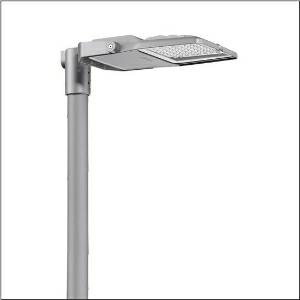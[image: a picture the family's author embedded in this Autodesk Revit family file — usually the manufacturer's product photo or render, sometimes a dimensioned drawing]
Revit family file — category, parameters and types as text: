
# Revit family: floodlight_fl_21_mini___pl43_5xa7772b4a3a_ae29
name_source: partatom
category: Lighting Fixtures
units: mm (PartAtom-declared; Revit-internal decimal feet)

## family parameters
Cut with Voids When Loaded = No
Host = Face
Light Source = No
Part Type = Normal
Room Calculation Point = No
Round Connector Dimension = Use Diameter
Shared = No

## types (1)
- --- (1 x LED, 6660 lm, 45.5 W, 4000K)
    Apparent Load = 46 VA
    CIE Flux Codes = 27 78 99 100 100
    Color Rendering = 70
    Color Temperature = 4000K
    Default Elevation = 1800 mm
    Description = Floodlight FL 21 mini, floodlight, primary light control with lens, of PMMA, primary optical cover: protective disc, of toughened safety glass, transparent, light distribution: PL43, light emission: direct distribution, installation type: surface-mounted, LED, High Power LED, rated luminous flux: 6.660lm, luminous efficacy: 146lm/W, light colour: 740, colour temperature: 4000K, control gear: ECG iQ, control: Auto-Match, Temp-Guard, Night-Set, Smart-Wire, Desk-Remote (wireless, voltage-free reading and setting of iQ features in the workshop via application-optimized NFC function/RFID function), optimised constant luminous flux control (CLO 2.0), Light-Fading, Lumen-Switch, with terminal, 6-pole, mains connection: 220..240V, AC, 50/60Hz, start of lifetime: 46W, end of lifetime: 48W, reduction: 22W, luminaire housing, of diecast aluminium, powder-coated, Siteco® metallic grey (DB 702S), corrosivity category C5 according to DIN EN ISO 12944, mast bracket, of steel, galvanised, powder-coated, protection rating (complete): IP66, insulation class (complete): insulation class II (safety insulation), certification: CE, ENEC, VDE, protection symbol: D, impact resistance: IK08, permissible operating ambient temperature: -40..+40°C, permissible operating ambient temperature for outdoor applications: -40..+50°C, standard: DIN EN 12944, packaging unit: 1 piece

Light Distribution: PL43
    Height = 70 mm
    Lamp = 1 x LED
    Lamp Light Flux = 6660 lm
    Lamp Power = 45.5 W
    Lamp count = 1
    Length = 485 mm
    Luminous efficacy = 146 lm/W
    Manufacturer = Siteco
    ModVariant = No
    Model = 5XA7772B4A3A
    Number of Poles = 1
    OnlyDefault = Yes
    Power Factor = 1
    Product Name = Floodlight FL 21 mini | PL43
    Product group = floodlight | pylon top
    ProductGroupID = 6101
    Protection Class = Protection class II
    Protection Degree = IP 66
    RLX_Detail_Level = 1
    RlxData = <blob elided: 100881 chars, md5=e329fee6>
    Socket = socket
    Standby Power = 0 W
    System Light Flux = 6660 lm
    System Power = 46 W
    Type Comments = factory setting: luminous flux: 100 % | dim-lin: 254 | 463 mA
    Type Image = l_1007125.jpg
    URL = http://relux.com
    VarID = @adj_073869
    Voltage = 0 V
    Weight = 0.00 kg
    Width = 337 mm

## geometry (parser evidence)
native form markers: Blend x4, Sweep x13
no freeform markers — native parametric forms only
